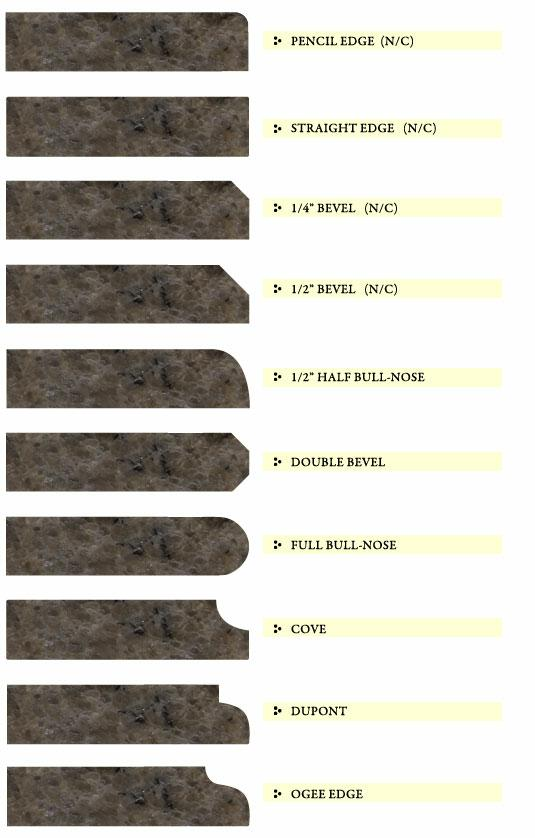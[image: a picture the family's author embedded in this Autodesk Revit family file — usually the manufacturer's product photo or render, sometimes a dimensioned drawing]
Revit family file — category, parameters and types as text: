
# Revit family: Casework-DuPont-Corian-Island-Countertop
name_source: partatom
category: Casework
revit_build: Autodesk Revit Architecture 2015 (Build: 20140903_1530(x64)
units: mm (PartAtom-declared; Revit-internal decimal feet)

## types (2) — shared parameters
1 2 Bevel = No
1 2 Half Bull Nose = No
1 4 Bevel = No
12B = No
12H = No
14B = No
C = No
Cove = No
D = No
DB = No
Description = Solid Surface Countertop
Double Bevel = No
Dupont = No
FBN = No
Full Bull Nose = No
Height = 3' - 0"
Manufacturer = DuPont
Model = Corian®
OE = No
Ogee Edge = No
PE = No
Pencil Edge = No
Product Name = Corian®
Product Page URL = http://www.dupont.com
SE = Yes
Straight Edge = Yes
zero-valued in all types: Cost

## per-type parameters (varying)
| type | Countertop Material | Depth | Thickness | URL |
| 3/4" | <By Category> | 2' - 0" | 0' - 0 3/4" | http://www.dupont.com |
| 1/2" | Solid Surface - DuPont - Corian - Glacier White 1/2" (12mm) | 4' - 0" | 0' - 0 1/2" | www.corian.com |

## geometry (parser evidence)
native form markers: Sweep x17
no freeform markers — native parametric forms only
